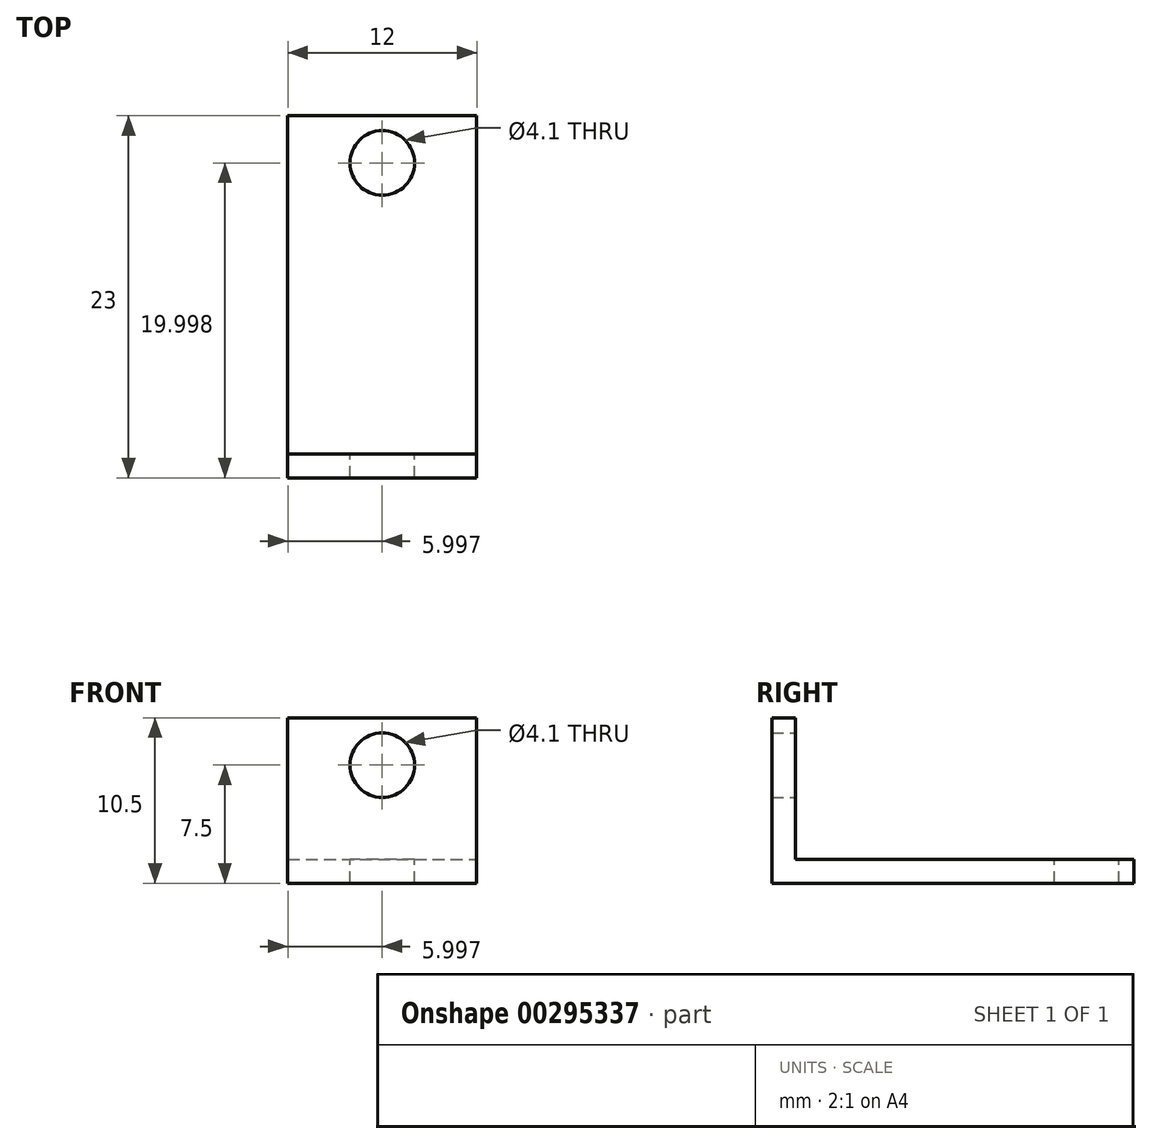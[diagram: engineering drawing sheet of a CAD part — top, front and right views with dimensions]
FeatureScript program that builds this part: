
annotation { "Feature Type Name" : "Feature", "Feature Type Description" : "" }
export const myFeature = defineFeature(function(context is Context, id is Id, definition is map)
    precondition{}
    {
        {
            var Q0;
            Q0=qCreatedBy(makeId("Top.planeOp"),FACE);
            var sketch = newSketch(context, id + "F0", { "sketchPlane" : qUnion([Q0])});
            skLineSegment(sketch, "E0.bottom", {"start": v(-23.32, 24.46) * mm, "end": v(-11.32, 24.46) * mm});
            skLineSegment(sketch, "E0.top", {"start": v(-23.32, 1.46) * mm, "end": v(-11.32, 1.46) * mm});
            skLineSegment(sketch, "E0.left", {"start": v(-23.32, 24.46) * mm, "end": v(-23.32, 1.46) * mm});
            skLineSegment(sketch, "E0.right", {"start": v(-11.32, 24.46) * mm, "end": v(-11.32, 1.46) * mm});
            skSolve(sketch);
        }
        {
            var Q0;
            Q0 = qSketchRegion(id + "F0", true);
            extrude(context, id + "F1", {"entities" : qUnion([Q0]), "depth" : 1.5 * mm, "offsetDistance" : 25 * mm});
        }
        {
            var Q0;
            Q0=makeQuery(id+"F1.opExtrude","CAP_FACE",FACE,{"disambiguationData":[OSD([sQuery(id+"F0.wireOp",EDGE,"E0.bottom"),sQuery(id+"F0.wireOp",EDGE,"E0.top"),sQuery(id+"F0.wireOp",EDGE,"E0.left"),sQuery(id+"F0.wireOp",EDGE,"E0.right")])],"isStart":false});
            var sketch = newSketch(context, id + "F2", { "sketchPlane" : qUnion([Q0])});
            skLineSegment(sketch, "E1", {"start": v(-17.32, 24.46) * mm, "end": v(-17.32, 21.46) * mm, "construction": true});
            skCircle(sketch, "E2", {"center": v(-17.32, 21.46) * mm, "radius": 2.05 * mm});
            skSolve(sketch);
        }
        {
            var Q0;
            Q0 = qSketchRegion(id + "F2", true);
            extrude(context, id + "F3", {"entities" : qUnion([Q0]), "operationType" : NewBodyOperationType.REMOVE, "oppositeDirection" : true, "depth" : 25 * mm, "offsetDistance" : 25 * mm});
        }
        {
            var Q0;
            Q0=makeQuery(id+"F1.opExtrude","CAP_FACE",FACE,{"disambiguationData":[OSD([sQuery(id+"F0.wireOp",EDGE,"E0.bottom"),sQuery(id+"F0.wireOp",EDGE,"E0.top"),sQuery(id+"F0.wireOp",EDGE,"E0.left"),sQuery(id+"F0.wireOp",EDGE,"E0.right")])],"isStart":false});
            var sketch = newSketch(context, id + "F4", { "sketchPlane" : qUnion([Q0])});
            skLineSegment(sketch, "E3.bottom", {"start": v(-23.32, 1.46) * mm, "end": v(-11.32, 1.46) * mm});
            skLineSegment(sketch, "E3.top", {"start": v(-23.32, 2.96) * mm, "end": v(-11.32, 2.96) * mm});
            skLineSegment(sketch, "E3.left", {"start": v(-23.32, 1.46) * mm, "end": v(-23.32, 2.96) * mm});
            skLineSegment(sketch, "E3.right", {"start": v(-11.32, 1.46) * mm, "end": v(-11.32, 2.96) * mm});
            skSolve(sketch);
        }
        {
            var Q0;
            Q0 = qSketchRegion(id + "F4", true);
            extrude(context, id + "F5", {"entities" : qUnion([Q0]), "operationType" : NewBodyOperationType.ADD, "depth" : 9 * mm, "offsetDistance" : 25 * mm});
        }
        {
            var Q0;
            Q0=makeQuery(id+"F5.opExtrude","SWEPT_FACE",FACE,{"disambiguationData":[OSD([sQuery(id+"F4.wireOp",EDGE,"E3.top")])]});
            var sketch = newSketch(context, id + "F6", { "sketchPlane" : qUnion([Q0])});
            skLineSegment(sketch, "E4", {"start": v(17.32, 10.5) * mm, "end": v(17.32, 7.5) * mm, "construction": true});
            skCircle(sketch, "E5", {"center": v(17.32, 7.5) * mm, "radius": 2.05 * mm});
            skSolve(sketch);
        }
        {
            var Q0;
            Q0 = qSketchRegion(id + "F6", true);
            extrude(context, id + "F7", {"entities" : qUnion([Q0]), "operationType" : NewBodyOperationType.REMOVE, "oppositeDirection" : true, "depth" : 25 * mm, "offsetDistance" : 25 * mm});
        }
    });
